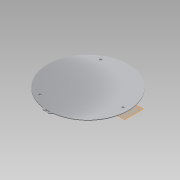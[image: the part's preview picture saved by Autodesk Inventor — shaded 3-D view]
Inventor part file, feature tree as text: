
AUTODESK INVENTOR PART (.ipt)
format: ipt  version: 2014 (Build 180170000, 170)  size: 171,520 bytes
history: native  units: mm
features: extrude x4, sketch x3, plane x1, chamfer x1, fillet x1, reference x1
ambient origin geometry x8: Origin, YZ Plane, XZ Plane, XY Plane, X Axis, Y Axis, Z Axis, Center Point
bodies: Solid1 (feature_tree)
feature tree (11):
  plane  "Work Plane1"
  extrude  "Extrusion1"  Depth=1.8mm TaperAngle=0.0deg
  extrude  "Extrusion2"  Depth=3.5mm
  chamfer  "Chamfer1"  Distance=10.0mm
  extrude  "Extrusion3"  Depth=2.0mm TaperAngle=45.0deg
  fillet  "Fillet1"  Radius=110.0mm
  extrude  "Extrusion4"  Depth=1.0mm
  sketch  "Sketch1"  dims[d0=252.0mm d1=1.8mm d2=0.0mm]
  reference  "Reference1"
  sketch  "Sketch3"  dims[d3=3.2mm d4=3.5mm]
  sketch  "Sketch4"  dims[d5=3.2mm d6=10.0mm d7=0.0mm d8=1.7mm d9=2.0mm d10=45.0deg d11=110.0mm d12=256.0mm d14=1.0mm d15=1.0mm d16=264.0mm d17=129.0mm d18=129.0mm d19=60.0deg d20=60.0deg d21=5.0mm d22=5.0mm d23=5.0mm d25=5.0mm d26=6.981317mm d27=6.981317mm d28=10.0mm d29=10.0mm d30=0.0mm d31=5.0mm d32=4.363323mm d33=15.0mm d34=15.0mm d35=2.0mm d36=115.0mm d37=1.0mm d38=0.0mm]
